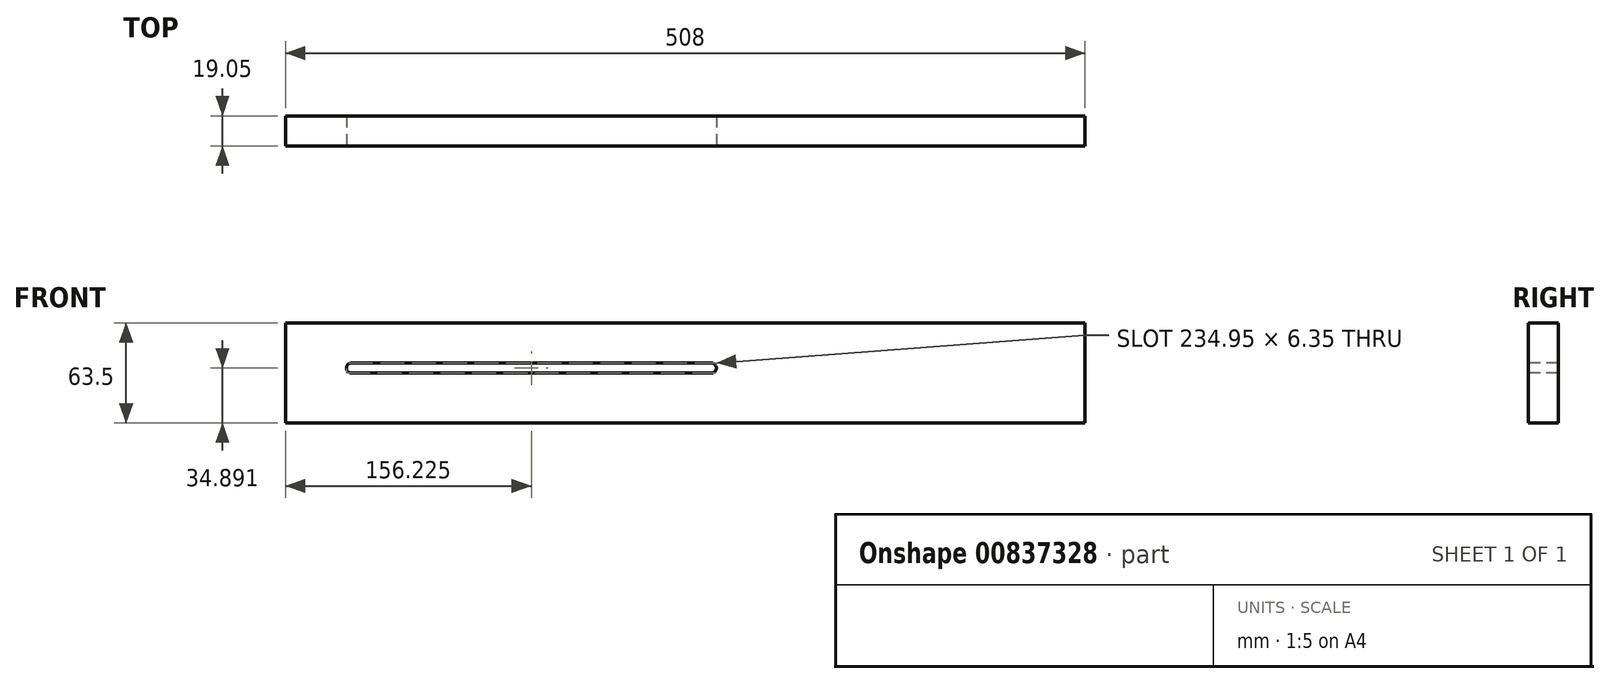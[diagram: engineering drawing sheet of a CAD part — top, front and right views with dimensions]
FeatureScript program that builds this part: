
annotation { "Feature Type Name" : "Feature", "Feature Type Description" : "" }
export const myFeature = defineFeature(function(context is Context, id is Id, definition is map)
    precondition{}
    {
        {
            var Q0;
            Q0=qCreatedBy(makeId("Front.planeOp"),FACE);
            var sketch = newSketch(context, id + "F0", { "sketchPlane" : qUnion([Q0])});
            skLineSegment(sketch, "E0.bottom", {"start": v(0, 0) * mm, "end": v(508, 0) * mm});
            skLineSegment(sketch, "E0.top", {"start": v(0, 63.5) * mm, "end": v(508, 63.5) * mm});
            skLineSegment(sketch, "E0.left", {"start": v(0, 0) * mm, "end": v(0, 63.5) * mm});
            skLineSegment(sketch, "E0.right", {"start": v(508, 0) * mm, "end": v(508, 63.5) * mm});
            skSolve(sketch);
        }
        {
            var Q0;
            Q0=makeQuery(id+"F0.imprint","IMPRINT",FACE,{"disambiguationData":[TD([[makeQuery(id+"F0.imprint","IMPRINT",EDGE,{"derivedFrom":sQuery(id+"F0.wireOp",EDGE,"E0.bottom")}),1.0]])]});
            extrude(context, id + "F1", {"entities" : qUnion([Q0]), "depth" : 19.05 * mm, "offsetDistance" : 25.4 * mm});
        }
        {
            var Q0;
            Q0=makeQuery(id+"F1.opExtrude","CAP_FACE",FACE,{"disambiguationData":[OSD([sQuery(id+"F0.wireOp",EDGE,"E0.bottom"),sQuery(id+"F0.wireOp",EDGE,"E0.top"),sQuery(id+"F0.wireOp",EDGE,"E0.left"),sQuery(id+"F0.wireOp",EDGE,"E0.right")])],"isStart":false});
            var sketch = newSketch(context, id + "F2", { "sketchPlane" : qUnion([Q0])});
            skLineSegment(sketch, "E1.bottom", {"start": v(41.92, 31.72) * mm, "end": v(270.52, 31.72) * mm});
            skLineSegment(sketch, "E1.top", {"start": v(41.92, 38.07) * mm, "end": v(270.52, 38.07) * mm});
            skLineSegment(sketch, "E1.left", {"start": v(41.92, 31.72) * mm, "end": v(41.92, 38.07) * mm});
            skLineSegment(sketch, "E1.right", {"start": v(270.52, 31.72) * mm, "end": v(270.52, 38.07) * mm});
            skArc(sketch, "E2", {"start": v(270.52, 31.72) * mm, "mid": v(273.7, 34.9) * mm, "end": v(270.52, 38.07) * mm});
            skArc(sketch, "E3", {"start": v(41.92, 38.07) * mm, "mid": v(38.75, 34.9) * mm, "end": v(41.92, 31.72) * mm});
            skSolve(sketch);
        }
        {
            var Q0;
            Q0=makeQuery(id+"F2.imprint","IMPRINT",FACE,{"disambiguationData":[TD([[makeQuery(id+"F2.imprint","IMPRINT",EDGE,{"derivedFrom":sQuery(id+"F2.wireOp",EDGE,"E1.bottom")}),1.0]])]});
            var Q1;
            Q1=makeQuery(id+"F2.imprint","IMPRINT",FACE,{"disambiguationData":[TD([[makeQuery(id+"F2.imprint","IMPRINT",EDGE,{"derivedFrom":sQuery(id+"F2.wireOp",EDGE,"E1.left")}),1.0]])]});
            var Q2;
            Q2=makeQuery(id+"F2.imprint","IMPRINT",FACE,{"disambiguationData":[TD([[makeQuery(id+"F2.imprint","IMPRINT",EDGE,{"derivedFrom":sQuery(id+"F2.wireOp",EDGE,"E1.right")}),-1.0]])]});
            extrude(context, id + "F3", {"entities" : qUnion([Q0, Q1, Q2]), "operationType" : NewBodyOperationType.REMOVE, "endBound" : BoundingType.THROUGH_ALL, "oppositeDirection" : true, "depth" : 25.4 * mm, "offsetDistance" : 25.4 * mm});
        }
    });
